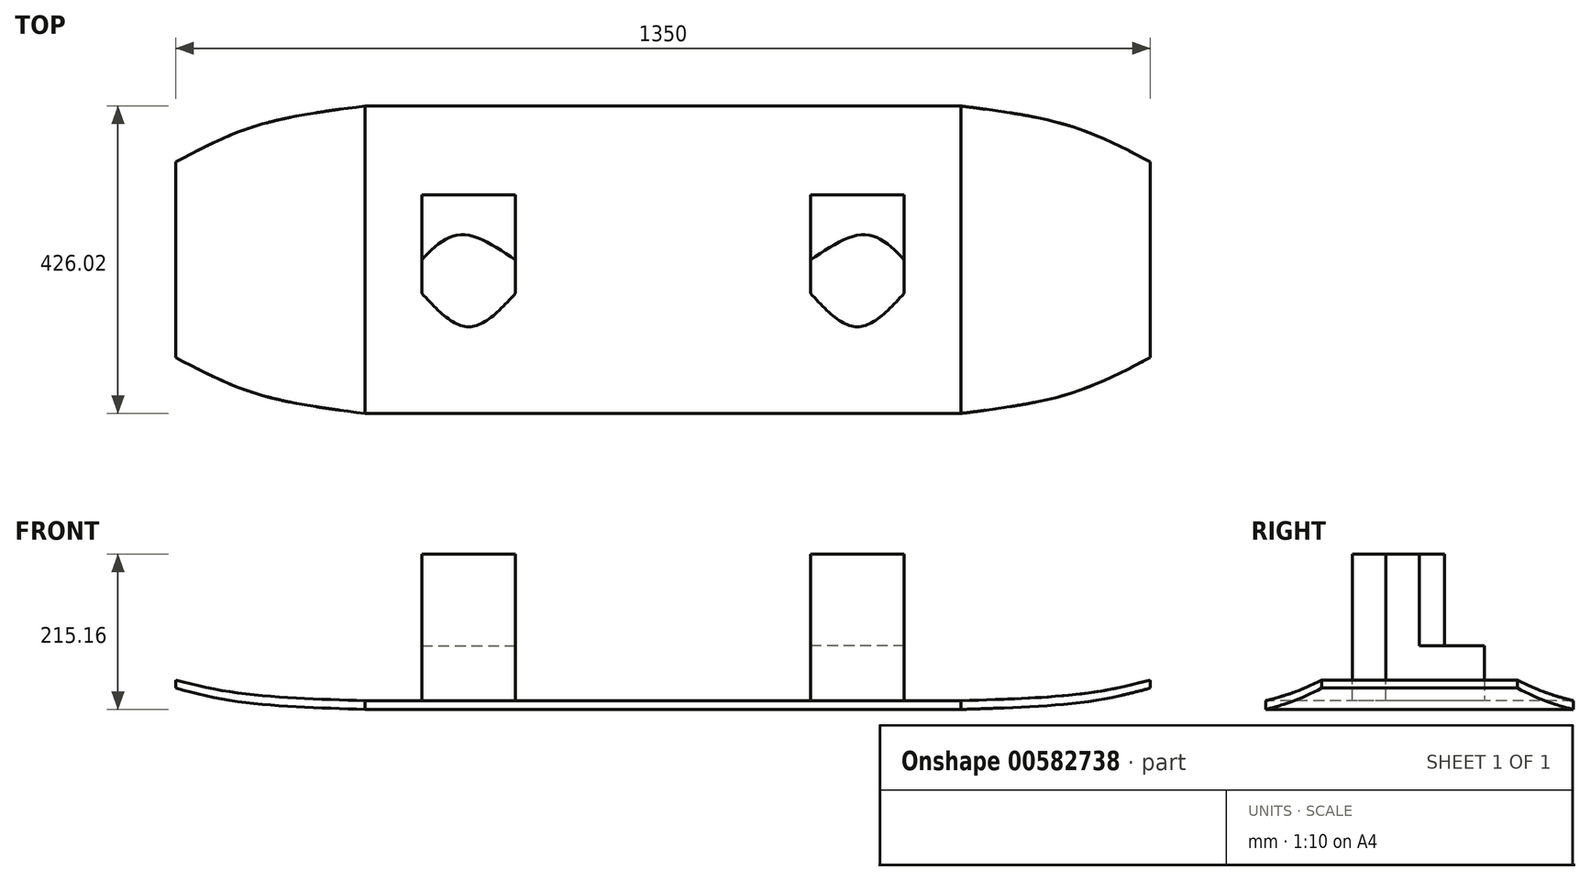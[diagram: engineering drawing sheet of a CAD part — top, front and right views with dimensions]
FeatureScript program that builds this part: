
annotation { "Feature Type Name" : "Feature", "Feature Type Description" : "" }
export const myFeature = defineFeature(function(context is Context, id is Id, definition is map)
    precondition{}
    {
        {
            var Q0;
            Q0=qCreatedBy(makeId("Front.planeOp"),FACE);
            var sketch = newSketch(context, id + "F0", { "sketchPlane" : qUnion([Q0])});
            skLineSegment(sketch, "E0.bottom", {"start": v(675, 50.8) * mm, "end": v(-675, 50.8) * mm});
            skLineSegment(sketch, "E0.top", {"start": v(675, -50.8) * mm, "end": v(-675, -50.8) * mm});
            skLineSegment(sketch, "E0.left", {"start": v(675, 50.8) * mm, "end": v(675, -50.8) * mm});
            skLineSegment(sketch, "E0.right", {"start": v(-675, 50.8) * mm, "end": v(-675, -50.8) * mm});
            skPoint(sketch, "E0.middle", {"position": v(0, 0) * mm});
            skSolve(sketch);
        }
        {
            var Q0;
            Q0 = qSketchRegion(id + "F0", true);
            extrude(context, id + "F1", {"entities" : qUnion([Q0]), "endBound" : BoundingType.SYMMETRIC, "depth" : 508 * mm, "offsetDistance" : 25.4 * mm});
        }
        {
            var Q0;
            Q0=makeQuery(id+"F1.opExtrude","CAP_FACE",FACE,{"disambiguationData":[OSD([sQuery(id+"F0.wireOp",EDGE,"E0.bottom"),sQuery(id+"F0.wireOp",EDGE,"E0.top"),sQuery(id+"F0.wireOp",EDGE,"E0.left"),sQuery(id+"F0.wireOp",EDGE,"E0.right")])],"isStart":false});
            var sketch = newSketch(context, id + "F2", { "sketchPlane" : qUnion([Q0])});
            skFitSpline(sketch, "E1", {"points": [v(-412.56, -50.8) * mm, v(-588.55, -39.89) * mm, v(-675, -21.24) * mm], "startDerivative": vector(-327.59, 10.93) * mm, "endDerivative": vector(-189.42, 50.44) * mm});
            skLineSegment(sketch, "E2", {"start": v(-675, -21.24) * mm, "end": v(-675, -50.8) * mm});
            skLineSegment(sketch, "E3", {"start": v(-412.56, -50.8) * mm, "end": v(-675, -50.8) * mm});
            skFitSpline(sketch, "E4.MirrorCS", {"points": [v(412.56, -50.8) * mm, v(588.55, -39.89) * mm, v(675, -21.24) * mm], "startDerivative": vector(327.59, 10.93) * mm, "endDerivative": vector(189.42, 50.44) * mm});
            skLineSegment(sketch, "E5.MirrorCS", {"start": v(412.56, -50.8) * mm, "end": v(675, -50.8) * mm});
            skLineSegment(sketch, "E6.MirrorCS", {"start": v(675, -21.24) * mm, "end": v(675, -50.8) * mm});
            skFitSpline(sketch, "E7", {"points": [v(-675, -10) * mm, v(-588.18, -28.13) * mm, v(-412.56, -38.84) * mm], "startDerivative": vector(190.16, -48.93) * mm, "endDerivative": vector(326.98, -10.9) * mm});
            skLineSegment(sketch, "E8", {"start": v(-675, -10) * mm, "end": v(-675, -21.24) * mm});
            skLineSegment(sketch, "E9", {"start": v(-675, -10) * mm, "end": v(-675, 50.8) * mm});
            skLineSegment(sketch, "E10", {"start": v(-675, 50.8) * mm, "end": v(675, 50.8) * mm});
            skLineSegment(sketch, "E11", {"start": v(675, 50.8) * mm, "end": v(675, -21.24) * mm});
            skFitSpline(sketch, "E12.MirrorCS", {"points": [v(675, -10) * mm, v(588.18, -28.13) * mm, v(412.56, -38.84) * mm], "startDerivative": vector(-190.16, -48.93) * mm, "endDerivative": vector(-326.98, -10.9) * mm});
            skLineSegment(sketch, "E13", {"start": v(-412.56, -38.84) * mm, "end": v(412.56, -38.84) * mm});
            skLineSegment(sketch, "E14", {"start": v(412.56, -50.8) * mm, "end": v(-412.56, -50.8) * mm});
            skSolve(sketch);
        }
        {
            var Q0;
            Q0=makeQuery(id+"F2.imprint","IMPRINT",FACE,{"disambiguationData":[TD([[makeQuery(id+"F2.imprint","IMPRINT",EDGE,{"derivedFrom":sQuery(id+"F2.wireOp",EDGE,"E7")}),1.0]])]});
            var Q1;
            Q1=makeQuery(id+"F2.imprint","IMPRINT",FACE,{"disambiguationData":[TD([[makeQuery(id+"F2.imprint","IMPRINT",EDGE,{"derivedFrom":sQuery(id+"F2.wireOp",EDGE,"E1")}),1.0]])]});
            var Q2;
            Q2=makeQuery(id+"F2.imprint","IMPRINT",FACE,{"disambiguationData":[TD([[makeQuery(id+"F2.imprint","IMPRINT",EDGE,{"derivedFrom":sQuery(id+"F2.wireOp",EDGE,"E4.MirrorCS")}),-1.0]])]});
            extrude(context, id + "F3", {"entities" : qUnion([Q0, Q1, Q2]), "operationType" : NewBodyOperationType.REMOVE, "oppositeDirection" : true, "depth" : 533.4 * mm, "offsetDistance" : 25.4 * mm});
        }
        {
            var Q0;
            Q0=qCreatedBy(makeId("Top.planeOp"),FACE);
            var sketch = newSketch(context, id + "F4", { "sketchPlane" : qUnion([Q0])});
            skLineSegment(sketch, "E15.0", {"start": v(-675, 254) * mm, "end": v(-675, -254) * mm});
            skFitSpline(sketch, "E16.0", {"points": [v(-675, 254) * mm, v(-648.68, 254) * mm, v(-585.3, 254) * mm, v(-476.3, 254) * mm, v(-412.56, 254) * mm]});
            skLineSegment(sketch, "E17.0", {"start": v(-412.56, 254) * mm, "end": v(-412.56, -254) * mm});
            skFitSpline(sketch, "E18.0", {"points": [v(-675, -254) * mm, v(-648.68, -254) * mm, v(-585.3, -254) * mm, v(-476.3, -254) * mm, v(-412.56, -254) * mm]});
            skLineSegment(sketch, "E19.0", {"start": v(-412.56, -254) * mm, "end": v(412.56, -254) * mm});
            skLineSegment(sketch, "E20.0", {"start": v(-412.56, 254) * mm, "end": v(412.56, 254) * mm});
            skPoint(sketch, "E21.0", {"position": v(544.79, 254) * mm});
            skFitSpline(sketch, "E22.0", {"points": [v(675, 254) * mm, v(648.68, 254) * mm, v(585.3, 254) * mm, v(476.3, 254) * mm, v(412.56, 254) * mm]});
            skLineSegment(sketch, "E23.0", {"start": v(675, 254) * mm, "end": v(675, -254) * mm});
            skFitSpline(sketch, "E24.0", {"points": [v(675, -254) * mm, v(648.68, -254) * mm, v(585.3, -254) * mm, v(476.3, -254) * mm, v(412.56, -254) * mm]});
            skFitSpline(sketch, "E25", {"points": [v(-412.56, 213.01) * mm, v(-564.17, 185.3) * mm, v(-675, 135.4) * mm], "startDerivative": vector(-299.64, -38.1) * mm, "endDerivative": vector(-223.73, -118.72) * mm});
            skFitSpline(sketch, "E26.MirrorCS", {"points": [v(-412.56, -213.01) * mm, v(-564.17, -185.3) * mm, v(-675, -135.4) * mm], "startDerivative": vector(-299.64, 38.1) * mm, "endDerivative": vector(-223.73, 118.72) * mm});
            skFitSpline(sketch, "E27.MirrorCS", {"points": [v(412.56, -213.01) * mm, v(564.17, -185.3) * mm, v(675, -135.4) * mm], "startDerivative": vector(299.64, 38.1) * mm, "endDerivative": vector(223.73, 118.72) * mm});
            skFitSpline(sketch, "E28.MirrorCS", {"points": [v(412.56, 213.01) * mm, v(564.17, 185.3) * mm, v(675, 135.4) * mm], "startDerivative": vector(299.64, -38.1) * mm, "endDerivative": vector(223.73, -118.72) * mm});
            skLineSegment(sketch, "E29", {"start": v(-412.56, -213.01) * mm, "end": v(412.56, -213.01) * mm});
            skLineSegment(sketch, "E30", {"start": v(412.56, 213.01) * mm, "end": v(-412.56, 213.01) * mm});
            skSolve(sketch);
        }
        {
            var Q0;
            {var subQ0=sQuery(id+"F4.wireOp",EDGE,"E20.0");Q0=makeQuery(id+"F4.imprint","IMPRINT",FACE,{"disambiguationData":[TD([[makeQuery(id+"F4.imprint","IMPRINT",EDGE,{"derivedFrom":subQ0}),-1.0]])]});}
            var Q1;
            {var subQ0=sQuery(id+"F4.wireOp",EDGE,"E19.0");Q1=makeQuery(id+"F4.imprint","IMPRINT",FACE,{"disambiguationData":[TD([[makeQuery(id+"F4.imprint","IMPRINT",EDGE,{"derivedFrom":subQ0}),1.0]])]});}
            var Q2;
            {var subQ0=sQuery(id+"F4.wireOp",EDGE,"E16.0");Q2=makeQuery(id+"F4.imprint","IMPRINT",FACE,{"disambiguationData":[TD([[makeQuery(id+"F4.imprint","IMPRINT",EDGE,{"derivedFrom":subQ0}),-1.0]])]});}
            var Q3;
            {var subQ0=sQuery(id+"F4.wireOp",EDGE,"E18.0");Q3=makeQuery(id+"F4.imprint","IMPRINT",FACE,{"disambiguationData":[TD([[makeQuery(id+"F4.imprint","IMPRINT",EDGE,{"derivedFrom":subQ0}),1.0]])]});}
            extrude(context, id + "F5", {"entities" : qUnion([Q0, Q1, Q2, Q3]), "operationType" : NewBodyOperationType.REMOVE, "oppositeDirection" : true, "depth" : 254 * mm, "offsetDistance" : 25.4 * mm});
        }
        {
            var Q0;
            Q0=makeQuery(id+"F3.boolean.opBoolean","COPY",FACE,{"derivedFrom":makeQuery(id+"F3.opExtrude","SWEPT_FACE",FACE,{"disambiguationData":[OSD([sQuery(id+"F2.wireOp",EDGE,"E13")])]})});
            var sketch = newSketch(context, id + "F6", { "sketchPlane" : qUnion([Q0])});
            skLineSegment(sketch, "E31.bottom", {"start": v(-334.24, 89.82) * mm, "end": v(-204.18, 89.82) * mm});
            skLineSegment(sketch, "E31.top", {"start": v(-334.24, -93.14) * mm, "end": v(-204.18, -93.14) * mm});
            skLineSegment(sketch, "E31.left", {"start": v(-334.24, 89.82) * mm, "end": v(-334.24, -93.14) * mm});
            skLineSegment(sketch, "E31.right", {"start": v(-204.18, 89.82) * mm, "end": v(-204.18, -93.14) * mm});
            skLineSegment(sketch, "E32.MirrorCS", {"start": v(334.24, 89.82) * mm, "end": v(204.18, 89.82) * mm});
            skLineSegment(sketch, "E33.MirrorCS", {"start": v(334.24, 89.82) * mm, "end": v(334.24, -93.14) * mm});
            skLineSegment(sketch, "E34.MirrorCS", {"start": v(334.24, -93.14) * mm, "end": v(204.18, -93.14) * mm});
            skLineSegment(sketch, "E35.MirrorCS", {"start": v(204.18, 89.82) * mm, "end": v(204.18, -93.14) * mm});
            skSolve(sketch);
        }
        {
            var Q0;
            Q0 = qSketchRegion(id + "F6", true);
            extrude(context, id + "F7", {"entities" : qUnion([Q0]), "operationType" : NewBodyOperationType.ADD, "depth" : 203.2 * mm, "offsetDistance" : 25.4 * mm});
        }
        {
            var Q0;
            Q0=makeQuery(id+"F7.opExtrude","CAP_FACE",FACE,{"disambiguationData":[OSD([sQuery(id+"F6.wireOp",EDGE,"E31.bottom"),sQuery(id+"F6.wireOp",EDGE,"E31.top"),sQuery(id+"F6.wireOp",EDGE,"E31.left"),sQuery(id+"F6.wireOp",EDGE,"E31.right")])],"isStart":false});
            var sketch = newSketch(context, id + "F8", { "sketchPlane" : qUnion([Q0])});
            skLineSegment(sketch, "E36.0", {"start": v(-334.24, -93.14) * mm, "end": v(-204.18, -93.14) * mm});
            skLineSegment(sketch, "E37.0", {"start": v(-334.24, 89.82) * mm, "end": v(-334.24, -93.14) * mm});
            skLineSegment(sketch, "E38.0", {"start": v(-204.18, 89.82) * mm, "end": v(-204.18, -93.14) * mm});
            skLineSegment(sketch, "E39.0.2", {"start": v(-204.18, -93.14) * mm, "end": v(-204.18, 89.82) * mm});
            skLineSegment(sketch, "E39.0.3", {"start": v(-204.18, 89.82) * mm, "end": v(-334.24, 89.82) * mm});
            skLineSegment(sketch, "E40.0.0", {"start": v(334.24, 89.82) * mm, "end": v(204.18, 89.82) * mm});
            skLineSegment(sketch, "E40.0.1", {"start": v(204.18, 89.82) * mm, "end": v(204.18, -93.14) * mm});
            skLineSegment(sketch, "E40.0.2", {"start": v(204.18, -93.14) * mm, "end": v(334.24, -93.14) * mm});
            skLineSegment(sketch, "E40.0.3", {"start": v(334.24, -93.14) * mm, "end": v(334.24, 89.82) * mm});
            skPoint(sketch, "E41.2.internal.snap0", {"position": v(-204.18, -1.66) * mm});
            skFitSpline(sketch, "E41", {"points": [v(-334.24, 0) * mm, v(-282.4, 34.7) * mm, v(-204.18, 0) * mm], "startDerivative": vector(105.08, 107.5) * mm, "endDerivative": vector(153.75, -101.99) * mm});
            skFitSpline(sketch, "E42.MirrorCS", {"points": [v(334.24, 0) * mm, v(282.4, 34.7) * mm, v(204.18, 0) * mm], "startDerivative": vector(-105.08, 107.5) * mm, "endDerivative": vector(-153.75, -101.99) * mm});
            skSolve(sketch);
        }
        {
            var Q0;
            {var subQ0=sQuery(id+"F8.wireOp",EDGE,"E39.0.3");Q0=makeQuery(id+"F8.imprint","IMPRINT",FACE,{"disambiguationData":[TD([[makeQuery(id+"F8.imprint","IMPRINT",EDGE,{"derivedFrom":subQ0}),-1.0]])]});}
            var Q1;
            {var subQ0=sQuery(id+"F8.wireOp",EDGE,"E40.0.0");Q1=makeQuery(id+"F8.imprint","IMPRINT",FACE,{"disambiguationData":[TD([[makeQuery(id+"F8.imprint","IMPRINT",EDGE,{"derivedFrom":subQ0}),1.0]])]});}
            extrude(context, id + "F9", {"entities" : qUnion([Q0, Q1]), "operationType" : NewBodyOperationType.REMOVE, "oppositeDirection" : true, "depth" : 127 * mm, "offsetDistance" : 25.4 * mm});
        }
        {
            var Q0;
            Q0=makeQuery(id+"F7.opExtrude","CAP_FACE",FACE,{"disambiguationData":[OSD([sQuery(id+"F6.wireOp",EDGE,"E31.bottom"),sQuery(id+"F6.wireOp",EDGE,"E31.top"),sQuery(id+"F6.wireOp",EDGE,"E31.left"),sQuery(id+"F6.wireOp",EDGE,"E31.right")])],"isStart":false});
            var sketch = newSketch(context, id + "F10", { "sketchPlane" : qUnion([Q0])});
            skFitSpline(sketch, "E43.0.0", {"points": [v(-204.18, 0) * mm, v(-231.83, 18.34) * mm, v(-283.08, 52.33) * mm, v(-318.1, 16.5) * mm, v(-334.24, 0) * mm]});
            skLineSegment(sketch, "E43.0.1", {"start": v(-334.24, 0) * mm, "end": v(-334.24, -93.14) * mm});
            skLineSegment(sketch, "E43.0.2", {"start": v(-334.24, -93.14) * mm, "end": v(-204.18, -93.14) * mm});
            skLineSegment(sketch, "E43.0.3", {"start": v(-204.18, -93.14) * mm, "end": v(-204.18, 0) * mm});
            skFitSpline(sketch, "E44", {"points": [v(-334.24, -46.57) * mm, v(-269.21, -93.14) * mm, v(-204.18, -46.57) * mm], "startDerivative": vector(130.05, -139.7) * mm, "endDerivative": vector(130.05, 139.7) * mm});
            skFitSpline(sketch, "E45.MirrorCS", {"points": [v(334.24, -46.57) * mm, v(269.21, -93.14) * mm, v(204.18, -46.57) * mm], "startDerivative": vector(-130.05, -139.7) * mm, "endDerivative": vector(-130.05, 139.7) * mm});
            skLineSegment(sketch, "E46.0.0", {"start": v(334.24, -93.14) * mm, "end": v(334.24, 0) * mm});
            skFitSpline(sketch, "E46.0.1", {"points": [v(334.24, 0) * mm, v(318.1, 16.5) * mm, v(283.08, 52.33) * mm, v(231.83, 18.34) * mm, v(204.18, 0) * mm]});
            skLineSegment(sketch, "E46.0.2", {"start": v(204.18, 0) * mm, "end": v(204.18, -93.14) * mm});
            skLineSegment(sketch, "E46.0.3", {"start": v(204.18, -93.14) * mm, "end": v(334.24, -93.14) * mm});
            skSolve(sketch);
        }
        {
            var Q0;
            {var subQ0=sQuery(id+"F10.wireOp",EDGE,"E43.0.3");var subQ1=sQuery(id+"F10.wireOp",EDGE,"E43.0.2");var subQ2=makeQuery(id+"F10.imprint","INTERSECT",VERTEX,{"derivedFrom":[subQ1,subQ0]});Q0=makeQuery(id+"F10.imprint","IMPRINT",FACE,{"disambiguationData":[TD([[makeQuery(id+"F10.imprint","IMPRINT",EDGE,{"disambiguationData":[TD([[subQ2,1.0]])],"derivedFrom":subQ1}),1.0]])]});}
            var Q1;
            {var subQ0=sQuery(id+"F10.wireOp",EDGE,"E43.0.2");var subQ1=sQuery(id+"F10.wireOp",EDGE,"E43.0.1");var subQ2=makeQuery(id+"F10.imprint","INTERSECT",VERTEX,{"derivedFrom":[subQ1,subQ0]});Q1=makeQuery(id+"F10.imprint","IMPRINT",FACE,{"disambiguationData":[TD([[makeQuery(id+"F10.imprint","IMPRINT",EDGE,{"disambiguationData":[TD([[subQ2,1.0]])],"derivedFrom":subQ1}),1.0]])]});}
            var Q2;
            {var subQ0=sQuery(id+"F10.wireOp",EDGE,"E46.0.0");var subQ1=sQuery(id+"F10.wireOp",EDGE,"E45.MirrorCS");var subQ2=makeQuery(id+"F10.imprint","INTERSECT",VERTEX,{"derivedFrom":[subQ1,subQ0]});Q2=makeQuery(id+"F10.imprint","IMPRINT",FACE,{"disambiguationData":[TD([[makeQuery(id+"F10.imprint","IMPRINT",EDGE,{"disambiguationData":[TD([[subQ2,-1.0]])],"derivedFrom":subQ1}),1.0]])]});}
            var Q3;
            {var subQ0=sQuery(id+"F10.wireOp",EDGE,"E46.0.2");var subQ1=sQuery(id+"F10.wireOp",EDGE,"E45.MirrorCS");var subQ2=makeQuery(id+"F10.imprint","INTERSECT",VERTEX,{"derivedFrom":[subQ1,subQ0]});Q3=makeQuery(id+"F10.imprint","IMPRINT",FACE,{"disambiguationData":[TD([[makeQuery(id+"F10.imprint","IMPRINT",EDGE,{"disambiguationData":[TD([[subQ2,1.0]])],"derivedFrom":subQ1}),1.0]])]});}
            extrude(context, id + "F11", {"entities" : qUnion([Q0, Q1, Q2, Q3]), "operationType" : NewBodyOperationType.REMOVE, "oppositeDirection" : true, "depth" : 203.2 * mm, "offsetDistance" : 25.4 * mm});
        }
    });
